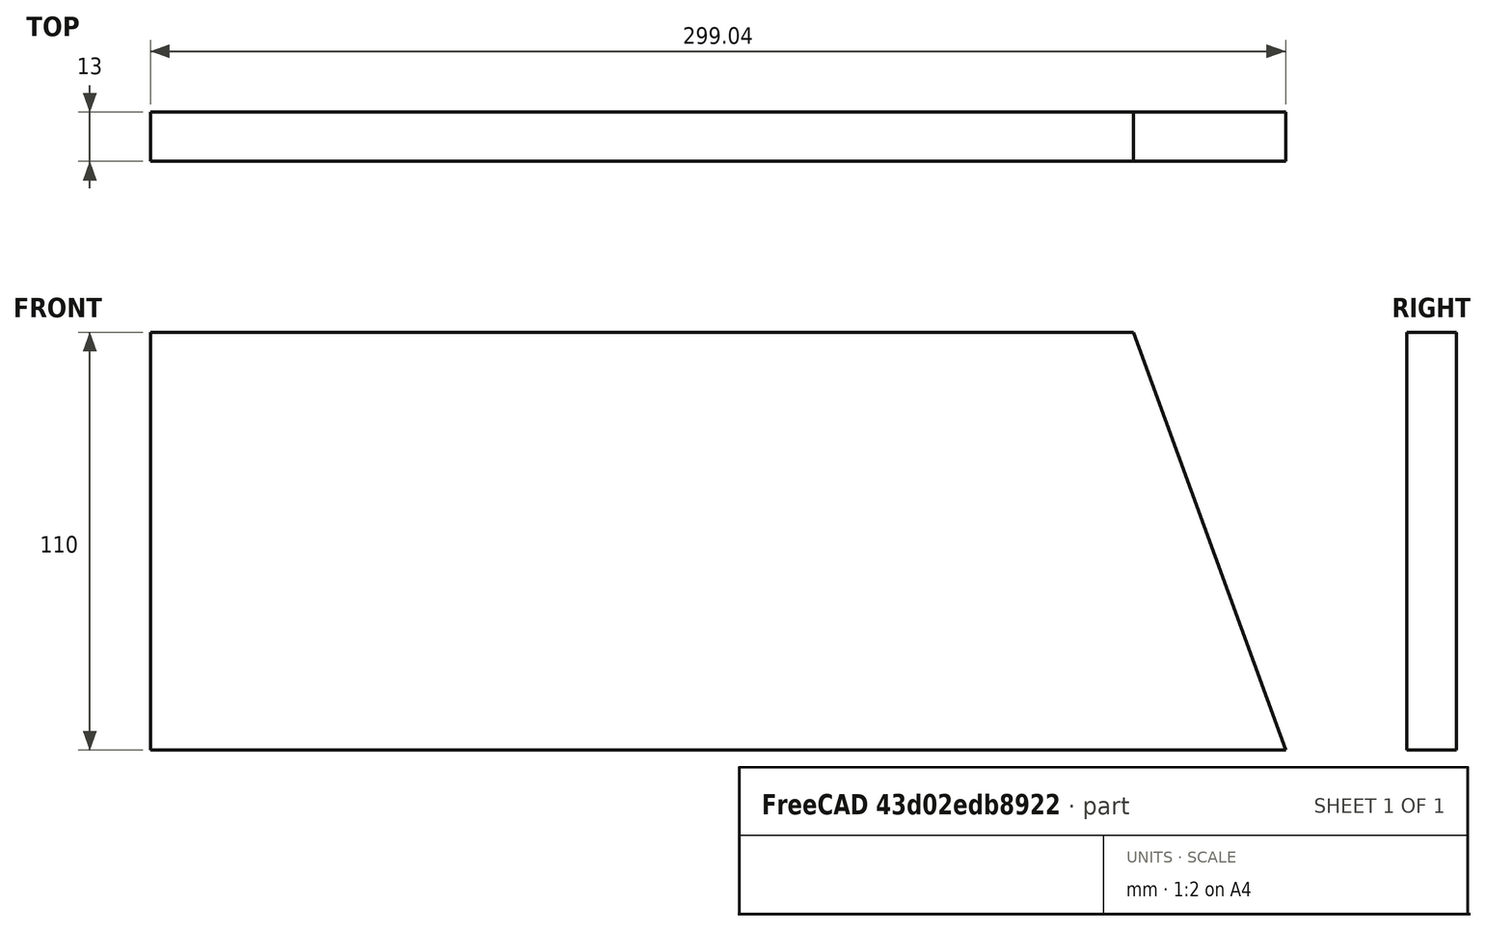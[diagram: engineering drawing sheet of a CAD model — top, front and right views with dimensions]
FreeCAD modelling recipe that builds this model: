
FCSTD DOCUMENT  (FreeCAD 0.18R14555 (Git shallow))
Label: 7001_Marquee_sidewall
License: All rights reserved
LicenseURL: http://en.wikipedia.org/wiki/All_rights_reserved
objects: Sketcher::SketchObject×1, PartDesign::Pad×1, PartDesign::Body×1, Spreadsheet::Sheet×1
note: 4 computed .brp shape members not serialized (recipe doc carries the construction recipe); baked Part::Feature solids carry a one-line shape summary decoded from their .brp

FEATURE [Sketcher::SketchObject] Sketch  label="SideWall"
  MapMode = 5
  Placement = pos=(0,0,0) rot=(1,0,0;1.5708rad)
  Support = -> [XZ_Plane]
  expr: Constraints[9] = xls.X0
  expr: Constraints.z_0 = xls.z_0
  sketch-geometry (4):
    g0: LineSegment StartX=299.037 StartY=0 StartZ=0 EndX=0 EndY=0 EndZ=0
    g1: LineSegment StartX=0 StartY=0 StartZ=0 EndX=0 EndY=110 EndZ=0
    g2: LineSegment StartX=0 StartY=110 StartZ=0 EndX=259 EndY=110 EndZ=0
    g3: LineSegment StartX=259 StartY=110 StartZ=0 EndX=299.037 EndY=0 EndZ=0
  constraints (11):
    c: Coincident(g0,g-1)
    c: Horizontal(g0)
    c: Coincident(g1,g-1)
    c: Vertical(g1)
    c: Coincident(g2,g1)
    c: Coincident(g0,g3)
    c: Perpendicular(g1,g2)
    c: DistanceY(g1,g1) = 110  'z_0'
    c: Coincident(g3,g2)
    c: DistanceX(g2,g2) = 259
    c: Angle(g3,g0) = 1.22173
FEATURE [PartDesign::Pad] Pad
  Length = 13
  Length2 = 13
  Placement = pos=(0,0,0) rot=(1,0,0;1.5708rad)
  Profile = -> Sketch
  Reversed = true
  Type = 0
FEATURE [PartDesign::Body] Body
  Group = -> [Sketch,Pad]
  Origin = -> Origin
  Tip = -> Pad
FEATURE [Spreadsheet::Sheet] Spreadsheet  label="xls"
  cells = C5=MARQUEE SIDEWALL ; C6=thickness of board; D6=t; E6(nt)=10; F6=mm; C8=Depth of Board; E8=255; G8=NOMINAL; C9=SIN 20 x Thickness; E9==E6 * sin(20); C10=Depth of board; D10=X0; E10(X0)==255 + 4; F10=mm; G10=REAL; C11=Height of board; D11=Z0; E11(z_0)=110; F11=mm
